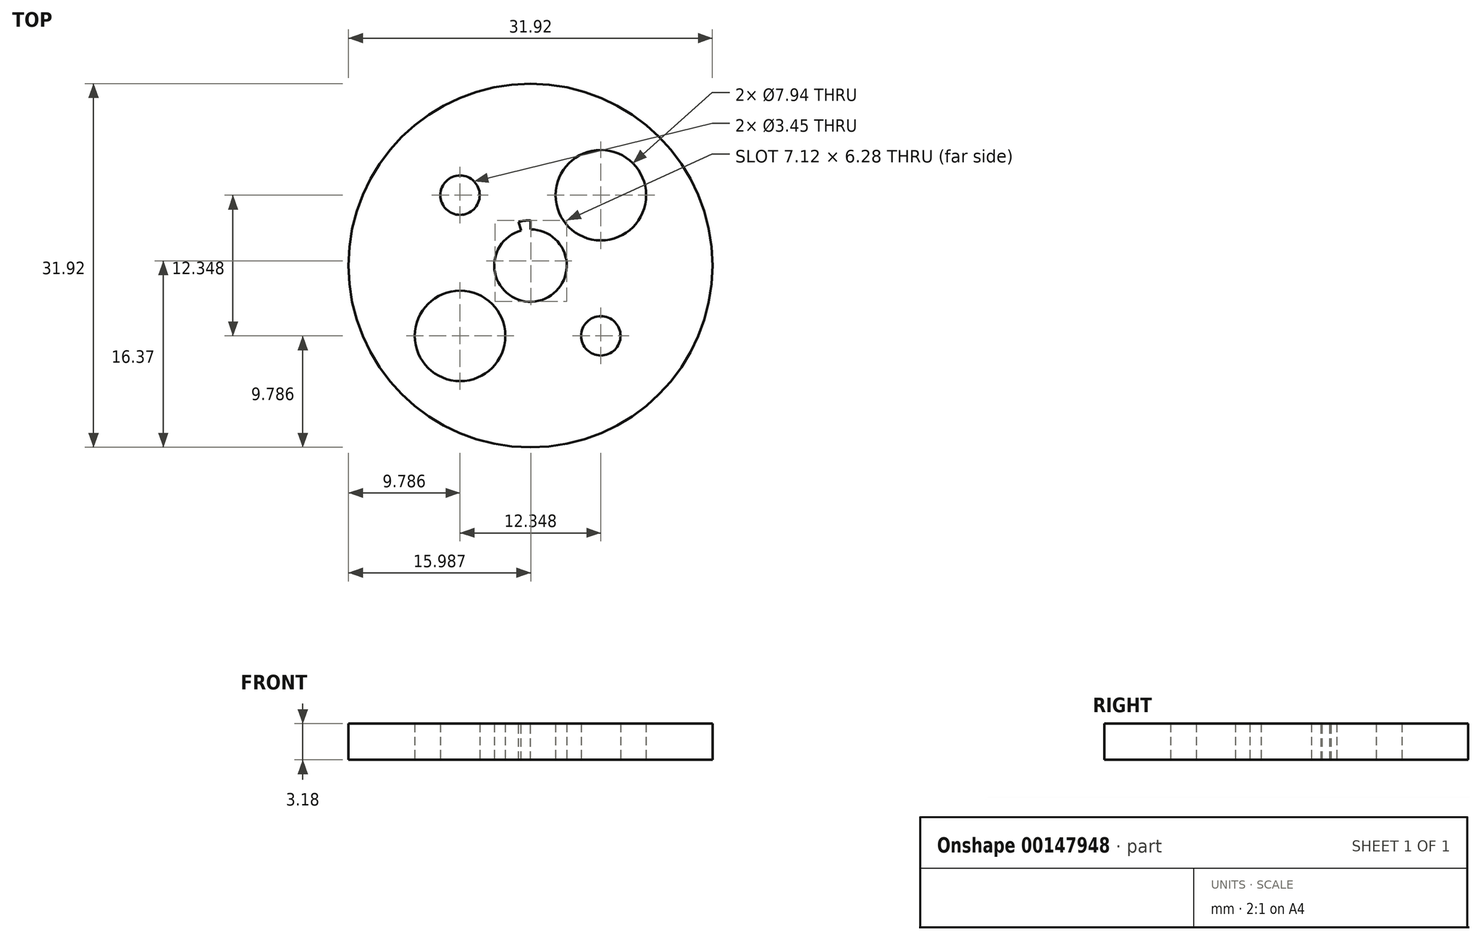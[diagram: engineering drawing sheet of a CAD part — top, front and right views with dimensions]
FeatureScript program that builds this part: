
annotation { "Feature Type Name" : "Feature", "Feature Type Description" : "" }
export const myFeature = defineFeature(function(context is Context, id is Id, definition is map)
    precondition{}
    {
        {
            var Q0;
            Q0=qCreatedBy(makeId("Top.planeOp"),FACE);
            var sketch = newSketch(context, id + "F0", { "sketchPlane" : qUnion([Q0])});
            skCircle(sketch, "E0", {"center": v(0, 0) * mm, "radius": 15.96 * mm});
            skCircle(sketch, "E1", {"center": v(0, 0) * mm, "radius": 3.18 * mm});
            skLineSegment(sketch, "E2.bottom", {"start": v(6.17, -6.17) * mm, "end": v(-6.17, -6.17) * mm, "construction": true});
            skLineSegment(sketch, "E2.top", {"start": v(6.17, 6.17) * mm, "end": v(-6.17, 6.17) * mm, "construction": true});
            skLineSegment(sketch, "E2.left", {"start": v(6.17, -6.17) * mm, "end": v(6.17, 6.17) * mm, "construction": true});
            skLineSegment(sketch, "E2.right", {"start": v(-6.17, -6.17) * mm, "end": v(-6.17, 6.17) * mm, "construction": true});
            skCircle(sketch, "E3", {"center": v(6.17, 6.17) * mm, "radius": 5.56 * mm, "construction": true});
            skCircle(sketch, "E4", {"center": v(6.17, 6.17) * mm, "radius": 3.97 * mm});
            skCircle(sketch, "E5", {"center": v(-6.17, -6.17) * mm, "radius": 3.97 * mm});
            skCircle(sketch, "E6", {"center": v(-6.17, 6.17) * mm, "radius": 1.73 * mm});
            skCircle(sketch, "E7", {"center": v(6.17, -6.17) * mm, "radius": 1.73 * mm});
            skSolve(sketch);
        }
        {
            var Q0;
            Q0=qSketchRegion(id+"F0",true);
            extrude(context, id + "F1", {"entities" : qUnion([Q0]), "depth" : 3.17 * mm});
        }
        {
            var Q0;
            Q0=makeQuery(id+"F1.opExtrude","CAP_FACE",FACE,{"disambiguationData":[OSD([sQuery(id+"F0.wireOp",EDGE,"E0"),sQuery(id+"F0.wireOp",EDGE,"E1"),sQuery(id+"F0.wireOp",EDGE,"E4"),sQuery(id+"F0.wireOp",EDGE,"E5"),sQuery(id+"F0.wireOp",EDGE,"E6"),sQuery(id+"F0.wireOp",EDGE,"E7")])],"isStart":false});
            var sketch = newSketch(context, id + "F2", { "sketchPlane" : qUnion([Q0])});
            skLineSegment(sketch, "E8", {"start": v(-0.82, 3.07) * mm, "end": v(-1.03, 3.83) * mm});
            skLineSegment(sketch, "E9", {"start": v(0, 3.18) * mm, "end": v(0, 3.97) * mm});
            skLineSegment(sketch, "E10", {"start": v(-0.82, 3.07) * mm, "end": v(0, 0) * mm, "construction": true});
            skLineSegment(sketch, "E11", {"start": v(0, 3.18) * mm, "end": v(0, 0) * mm, "construction": true});
            skArc(sketch, "E12", {"start": v(0, 3.97) * mm, "mid": v(-0.52, 3.93) * mm, "end": v(-1.03, 3.83) * mm});
            skArc(sketch, "E13", {"start": v(0, 3.18) * mm, "mid": v(-0.41, 3.15) * mm, "end": v(-0.82, 3.07) * mm});
            skSolve(sketch);
        }
        {
            var Q0;
            Q0=qSketchRegion(id+"F2",true);
            var Q1;
            Q1=makeQuery(id+"F1.opExtrude","CAP_FACE",FACE,{"disambiguationData":[OSD([sQuery(id+"F0.wireOp",EDGE,"E0"),sQuery(id+"F0.wireOp",EDGE,"E1"),sQuery(id+"F0.wireOp",EDGE,"E4"),sQuery(id+"F0.wireOp",EDGE,"E5"),sQuery(id+"F0.wireOp",EDGE,"E6"),sQuery(id+"F0.wireOp",EDGE,"E7")])],"isStart":true});
            extrude(context, id + "F3", {"entities" : qUnion([Q0]), "operationType" : NewBodyOperationType.REMOVE, "endBound" : BoundingType.UP_TO_SURFACE, "oppositeDirection" : true, "endBoundEntityFace" : qUnion([Q1]), "depth" : 25.4 * mm});
        }
    });
